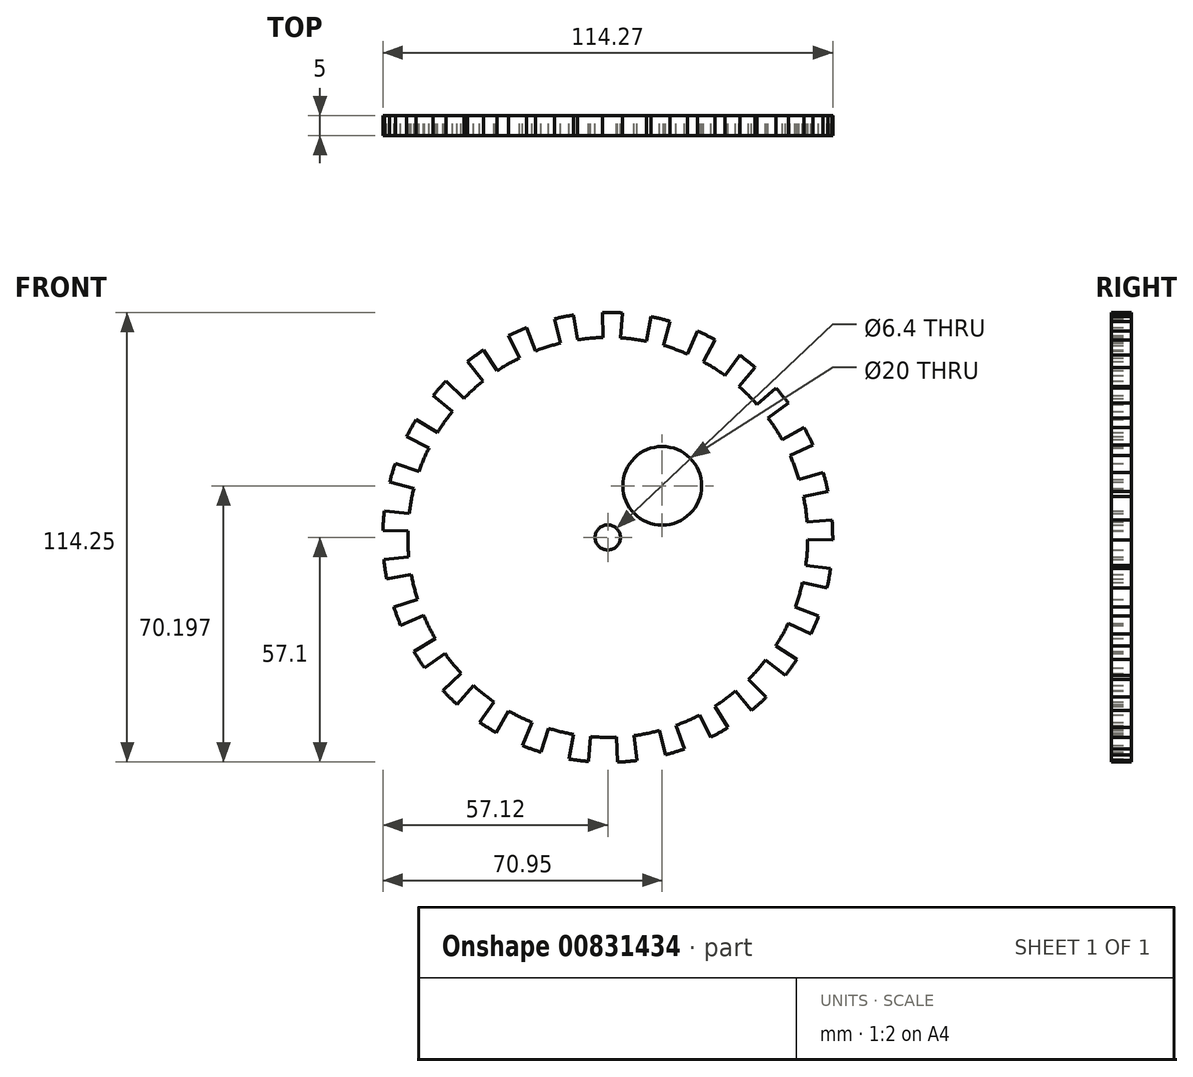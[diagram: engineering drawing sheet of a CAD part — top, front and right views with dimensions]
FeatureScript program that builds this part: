
annotation { "Feature Type Name" : "Feature", "Feature Type Description" : "" }
export const myFeature = defineFeature(function(context is Context, id is Id, definition is map)
    precondition{}
    {
        {
            var Q0;
            Q0=qCreatedBy(makeId("Front.planeOp"),FACE);
            var sketch = newSketch(context, id + "F0", { "sketchPlane" : qUnion([Q0])});
            skArc(sketch, "E0", {"start": v(15.87, 54.9) * mm, "mid": v(13.45, 55.55) * mm, "end": v(11, 56.08) * mm});
            skCircle(sketch, "E1", {"center": v(0, 0) * mm, "radius": 50.8 * mm});
            skLineSegment(sketch, "E2", {"start": v(14.1, 48.8) * mm, "end": v(15.87, 54.9) * mm});
            skLineSegment(sketch, "E3", {"start": v(9.78, 49.85) * mm, "end": v(11, 56.08) * mm});
            skArc(sketch, "E4.1.0", {"start": v(3.7, 57.03) * mm, "mid": v(1.2, 57.14) * mm, "end": v(-1.3, 57.14) * mm});
            skLineSegment(sketch, "E4.1.1", {"start": v(3.28, 50.7) * mm, "end": v(3.7, 57.03) * mm});
            skLineSegment(sketch, "E4.1.2", {"start": v(-1.16, 50.79) * mm, "end": v(-1.3, 57.14) * mm});
            skArc(sketch, "E4.2.0", {"start": v(-8.65, 56.5) * mm, "mid": v(-11.12, 56.06) * mm, "end": v(-13.56, 55.52) * mm});
            skLineSegment(sketch, "E4.2.1", {"start": v(-7.7, 50.21) * mm, "end": v(-8.65, 56.5) * mm});
            skLineSegment(sketch, "E4.2.2", {"start": v(-12.05, 49.35) * mm, "end": v(-13.56, 55.52) * mm});
            skArc(sketch, "E4.3.0", {"start": v(-20.6, 53.3) * mm, "mid": v(-22.9, 52.36) * mm, "end": v(-25.18, 51.3) * mm});
            skLineSegment(sketch, "E4.3.1", {"start": v(-18.3, 47.39) * mm, "end": v(-20.6, 53.3) * mm});
            skLineSegment(sketch, "E4.3.2", {"start": v(-22.38, 45.6) * mm, "end": v(-25.18, 51.3) * mm});
            skArc(sketch, "E4.4.0", {"start": v(-31.57, 47.64) * mm, "mid": v(-33.63, 46.2) * mm, "end": v(-35.62, 44.7) * mm});
            skLineSegment(sketch, "E4.4.1", {"start": v(-28.07, 42.34) * mm, "end": v(-31.57, 47.64) * mm});
            skLineSegment(sketch, "E4.4.2", {"start": v(-31.66, 39.73) * mm, "end": v(-35.62, 44.7) * mm});
            skArc(sketch, "E4.5.0", {"start": v(-41.08, 39.73) * mm, "mid": v(-42.78, 37.9) * mm, "end": v(-44.4, 36) * mm});
            skLineSegment(sketch, "E4.5.1", {"start": v(-36.51, 35.32) * mm, "end": v(-41.08, 39.73) * mm});
            skLineSegment(sketch, "E4.5.2", {"start": v(-39.46, 32) * mm, "end": v(-44.4, 36) * mm});
            skArc(sketch, "E4.6.0", {"start": v(-48.66, 29.98) * mm, "mid": v(-49.92, 27.82) * mm, "end": v(-51.1, 25.6) * mm});
            skLineSegment(sketch, "E4.6.1", {"start": v(-43.25, 26.65) * mm, "end": v(-48.66, 29.98) * mm});
            skLineSegment(sketch, "E4.6.2", {"start": v(-45.41, 22.76) * mm, "end": v(-51.1, 25.6) * mm});
            skArc(sketch, "E4.7.0", {"start": v(-53.96, 18.81) * mm, "mid": v(-54.74, 16.44) * mm, "end": v(-55.4, 14.03) * mm});
            skLineSegment(sketch, "E4.7.1", {"start": v(-47.97, 16.72) * mm, "end": v(-53.96, 18.81) * mm});
            skLineSegment(sketch, "E4.7.2", {"start": v(-49.25, 12.47) * mm, "end": v(-55.4, 14.03) * mm});
            skArc(sketch, "E4.8.0", {"start": v(-56.75, 6.77) * mm, "mid": v(-56.99, 4.29) * mm, "end": v(-57.12, 1.79) * mm});
            skLineSegment(sketch, "E4.8.1", {"start": v(-50.44, 6.02) * mm, "end": v(-56.75, 6.77) * mm});
            skLineSegment(sketch, "E4.8.2", {"start": v(-50.78, 1.59) * mm, "end": v(-57.12, 1.79) * mm});
            skArc(sketch, "E4.9.0", {"start": v(-56.88, -5.58) * mm, "mid": v(-56.58, -8.07) * mm, "end": v(-56.17, -10.53) * mm});
            skLineSegment(sketch, "E4.9.1", {"start": v(-50.56, -4.96) * mm, "end": v(-56.88, -5.58) * mm});
            skLineSegment(sketch, "E4.9.2", {"start": v(-49.93, -9.36) * mm, "end": v(-56.17, -10.53) * mm});
            skArc(sketch, "E4.10.0", {"start": v(-54.35, -17.68) * mm, "mid": v(-53.52, -20.04) * mm, "end": v(-52.6, -22.36) * mm});
            skLineSegment(sketch, "E4.10.1", {"start": v(-48.3, -15.71) * mm, "end": v(-54.35, -17.68) * mm});
            skLineSegment(sketch, "E4.10.2", {"start": v(-46.75, -19.88) * mm, "end": v(-52.6, -22.36) * mm});
            skArc(sketch, "E4.11.0", {"start": v(-49.28, -28.95) * mm, "mid": v(-47.96, -31.08) * mm, "end": v(-46.56, -33.15) * mm});
            skLineSegment(sketch, "E4.11.1", {"start": v(-43.8, -25.73) * mm, "end": v(-49.28, -28.95) * mm});
            skLineSegment(sketch, "E4.11.2", {"start": v(-41.38, -29.46) * mm, "end": v(-46.56, -33.15) * mm});
            skArc(sketch, "E4.12.0", {"start": v(-41.9, -38.86) * mm, "mid": v(-40.16, -40.66) * mm, "end": v(-38.34, -42.38) * mm});
            skLineSegment(sketch, "E4.12.1", {"start": v(-37.24, -34.55) * mm, "end": v(-41.9, -38.86) * mm});
            skLineSegment(sketch, "E4.12.2", {"start": v(-34.08, -37.67) * mm, "end": v(-38.34, -42.38) * mm});
            skArc(sketch, "E4.13.0", {"start": v(-32.57, -46.96) * mm, "mid": v(-30.48, -48.34) * mm, "end": v(-28.34, -49.63) * mm});
            skLineSegment(sketch, "E4.13.1", {"start": v(-28.95, -41.75) * mm, "end": v(-32.57, -46.96) * mm});
            skLineSegment(sketch, "E4.13.2", {"start": v(-25.19, -44.12) * mm, "end": v(-28.34, -49.63) * mm});
            skArc(sketch, "E4.14.0", {"start": v(-21.7, -52.87) * mm, "mid": v(-19.38, -53.77) * mm, "end": v(-17, -54.56) * mm});
            skLineSegment(sketch, "E4.14.1", {"start": v(-19.3, -47) * mm, "end": v(-21.7, -52.87) * mm});
            skLineSegment(sketch, "E4.14.2", {"start": v(-15.12, -48.5) * mm, "end": v(-17, -54.56) * mm});
            skArc(sketch, "E4.15.0", {"start": v(-9.84, -56.3) * mm, "mid": v(-7.36, -56.67) * mm, "end": v(-4.88, -56.94) * mm});
            skLineSegment(sketch, "E4.15.1", {"start": v(-8.74, -50.04) * mm, "end": v(-9.84, -56.3) * mm});
            skLineSegment(sketch, "E4.15.2", {"start": v(-4.34, -50.61) * mm, "end": v(-4.88, -56.94) * mm});
            skArc(sketch, "E4.16.0", {"start": v(2.5, -57.1) * mm, "mid": v(5, -56.93) * mm, "end": v(7.48, -56.66) * mm});
            skLineSegment(sketch, "E4.16.1", {"start": v(2.22, -50.75) * mm, "end": v(2.5, -57.1) * mm});
            skLineSegment(sketch, "E4.16.2", {"start": v(6.65, -50.36) * mm, "end": v(7.48, -56.66) * mm});
            skArc(sketch, "E4.17.0", {"start": v(14.71, -55.22) * mm, "mid": v(17.11, -54.53) * mm, "end": v(19.48, -53.73) * mm});
            skLineSegment(sketch, "E4.17.1", {"start": v(13.08, -49.09) * mm, "end": v(14.71, -55.22) * mm});
            skLineSegment(sketch, "E4.17.2", {"start": v(17.32, -47.76) * mm, "end": v(19.48, -53.73) * mm});
            skArc(sketch, "E4.18.0", {"start": v(26.24, -50.77) * mm, "mid": v(28.43, -49.57) * mm, "end": v(30.58, -48.28) * mm});
            skLineSegment(sketch, "E4.18.1", {"start": v(23.32, -45.13) * mm, "end": v(26.24, -50.77) * mm});
            skLineSegment(sketch, "E4.18.2", {"start": v(27.18, -42.92) * mm, "end": v(30.58, -48.28) * mm});
            skArc(sketch, "E4.19.0", {"start": v(36.54, -43.94) * mm, "mid": v(38.43, -42.3) * mm, "end": v(40.24, -40.58) * mm});
            skLineSegment(sketch, "E4.19.1", {"start": v(32.48, -39.06) * mm, "end": v(36.54, -43.94) * mm});
            skLineSegment(sketch, "E4.19.2", {"start": v(35.77, -36.07) * mm, "end": v(40.24, -40.58) * mm});
            skArc(sketch, "E4.20.0", {"start": v(45.13, -35.06) * mm, "mid": v(46.62, -33.05) * mm, "end": v(48.02, -30.98) * mm});
            skLineSegment(sketch, "E4.20.1", {"start": v(40.12, -31.17) * mm, "end": v(45.13, -35.06) * mm});
            skLineSegment(sketch, "E4.20.2", {"start": v(42.69, -27.54) * mm, "end": v(48.02, -30.98) * mm});
            skArc(sketch, "E4.21.0", {"start": v(51.61, -24.54) * mm, "mid": v(52.64, -22.26) * mm, "end": v(53.56, -19.93) * mm});
            skLineSegment(sketch, "E4.21.1", {"start": v(45.88, -21.81) * mm, "end": v(51.61, -24.54) * mm});
            skLineSegment(sketch, "E4.21.2", {"start": v(47.6, -17.72) * mm, "end": v(53.56, -19.93) * mm});
            skArc(sketch, "E4.22.0", {"start": v(55.68, -12.87) * mm, "mid": v(56.2, -10.42) * mm, "end": v(56.6, -7.95) * mm});
            skLineSegment(sketch, "E4.22.1", {"start": v(49.5, -11.44) * mm, "end": v(55.68, -12.87) * mm});
            skLineSegment(sketch, "E4.22.2", {"start": v(50.3, -7.07) * mm, "end": v(56.6, -7.95) * mm});
            skArc(sketch, "E4.23.0", {"start": v(57.15, -0.6) * mm, "mid": v(57.12, 1.9) * mm, "end": v(56.98, 4.4) * mm});
            skLineSegment(sketch, "E4.23.1", {"start": v(50.8, -0.53) * mm, "end": v(57.15, -0.6) * mm});
            skLineSegment(sketch, "E4.23.2", {"start": v(50.65, 3.9) * mm, "end": v(56.98, 4.4) * mm});
            skArc(sketch, "E4.24.0", {"start": v(55.94, 11.7) * mm, "mid": v(55.37, 14.14) * mm, "end": v(54.7, 16.54) * mm});
            skLineSegment(sketch, "E4.24.1", {"start": v(49.72, 10.4) * mm, "end": v(55.94, 11.7) * mm});
            skLineSegment(sketch, "E4.24.2", {"start": v(48.62, 14.7) * mm, "end": v(54.7, 16.54) * mm});
            skArc(sketch, "E4.25.0", {"start": v(52.12, 23.45) * mm, "mid": v(51.04, 25.7) * mm, "end": v(49.87, 27.92) * mm});
            skLineSegment(sketch, "E4.25.1", {"start": v(46.33, 20.85) * mm, "end": v(52.12, 23.45) * mm});
            skLineSegment(sketch, "E4.25.2", {"start": v(44.33, 24.82) * mm, "end": v(49.87, 27.92) * mm});
            skArc(sketch, "E4.26.0", {"start": v(45.86, 34.1) * mm, "mid": v(44.32, 36.08) * mm, "end": v(42.7, 37.98) * mm});
            skLineSegment(sketch, "E4.26.1", {"start": v(40.76, 30.32) * mm, "end": v(45.86, 34.1) * mm});
            skLineSegment(sketch, "E4.26.2", {"start": v(37.96, 33.76) * mm, "end": v(42.7, 37.98) * mm});
            skArc(sketch, "E4.27.0", {"start": v(37.45, 43.17) * mm, "mid": v(35.53, 44.76) * mm, "end": v(33.54, 46.28) * mm});
            skLineSegment(sketch, "E4.27.1", {"start": v(33.3, 38.37) * mm, "end": v(37.45, 43.17) * mm});
            skLineSegment(sketch, "E4.27.2", {"start": v(29.81, 41.13) * mm, "end": v(33.54, 46.28) * mm});
            skArc(sketch, "E4.28.0", {"start": v(27.3, 50.2) * mm, "mid": v(25.07, 51.36) * mm, "end": v(22.8, 52.4) * mm});
            skLineSegment(sketch, "E4.28.1", {"start": v(24.26, 44.63) * mm, "end": v(27.3, 50.2) * mm});
            skLineSegment(sketch, "E4.28.2", {"start": v(20.27, 46.58) * mm, "end": v(22.8, 52.4) * mm});
            skCircle(sketch, "E5", {"center": v(13.83, 13.1) * mm, "radius": 10 * mm});
            skCircle(sketch, "E6", {"center": v(0, 0) * mm, "radius": 3.2 * mm});
            skSolve(sketch);
        }
        {
            var Q0;
            Q0=makeQuery(id+"F0.imprint","IMPRINT",FACE,{"disambiguationData":[TD([[makeQuery(id+"F0.imprint","IMPRINT",EDGE,{"derivedFrom":sQuery(id+"F0.wireOp",EDGE,"E0")}),1.0]])]});
            var Q1;
            Q1=makeQuery(id+"F0.imprint","IMPRINT",FACE,{"disambiguationData":[TD([[makeQuery(id+"F0.imprint","IMPRINT",EDGE,{"derivedFrom":sQuery(id+"F0.wireOp",EDGE,"E4.24.0")}),1.0]])]});
            var Q2;
            Q2=makeQuery(id+"F0.imprint","IMPRINT",FACE,{"disambiguationData":[TD([[makeQuery(id+"F0.imprint","IMPRINT",EDGE,{"derivedFrom":sQuery(id+"F0.wireOp",EDGE,"E4.25.0")}),1.0]])]});
            var Q3;
            Q3=makeQuery(id+"F0.imprint","IMPRINT",FACE,{"disambiguationData":[TD([[makeQuery(id+"F0.imprint","IMPRINT",EDGE,{"derivedFrom":sQuery(id+"F0.wireOp",EDGE,"E4.26.0")}),1.0]])]});
            var Q4;
            Q4=makeQuery(id+"F0.imprint","IMPRINT",FACE,{"disambiguationData":[TD([[makeQuery(id+"F0.imprint","IMPRINT",EDGE,{"derivedFrom":sQuery(id+"F0.wireOp",EDGE,"E4.27.0")}),1.0]])]});
            var Q5;
            Q5=makeQuery(id+"F0.imprint","IMPRINT",FACE,{"disambiguationData":[TD([[makeQuery(id+"F0.imprint","IMPRINT",EDGE,{"derivedFrom":sQuery(id+"F0.wireOp",EDGE,"E4.28.0")}),1.0]])]});
            var Q6;
            Q6=makeQuery(id+"F0.imprint","IMPRINT",FACE,{"disambiguationData":[TD([[makeQuery(id+"F0.imprint","IMPRINT",EDGE,{"derivedFrom":sQuery(id+"F0.wireOp",EDGE,"E4.1.0")}),1.0]])]});
            var Q7;
            Q7=makeQuery(id+"F0.imprint","IMPRINT",FACE,{"disambiguationData":[TD([[makeQuery(id+"F0.imprint","IMPRINT",EDGE,{"derivedFrom":sQuery(id+"F0.wireOp",EDGE,"E4.2.0")}),1.0]])]});
            var Q8;
            Q8=makeQuery(id+"F0.imprint","IMPRINT",FACE,{"disambiguationData":[TD([[makeQuery(id+"F0.imprint","IMPRINT",EDGE,{"derivedFrom":sQuery(id+"F0.wireOp",EDGE,"E4.3.0")}),1.0]])]});
            var Q9;
            Q9=makeQuery(id+"F0.imprint","IMPRINT",FACE,{"disambiguationData":[TD([[makeQuery(id+"F0.imprint","IMPRINT",EDGE,{"derivedFrom":sQuery(id+"F0.wireOp",EDGE,"E4.4.0")}),1.0]])]});
            var Q10;
            Q10=makeQuery(id+"F0.imprint","IMPRINT",FACE,{"disambiguationData":[TD([[makeQuery(id+"F0.imprint","IMPRINT",EDGE,{"derivedFrom":sQuery(id+"F0.wireOp",EDGE,"E4.5.0")}),1.0]])]});
            var Q11;
            Q11=makeQuery(id+"F0.imprint","IMPRINT",FACE,{"disambiguationData":[TD([[makeQuery(id+"F0.imprint","IMPRINT",EDGE,{"derivedFrom":sQuery(id+"F0.wireOp",EDGE,"E4.6.0")}),1.0]])]});
            var Q12;
            Q12=makeQuery(id+"F0.imprint","IMPRINT",FACE,{"disambiguationData":[TD([[makeQuery(id+"F0.imprint","IMPRINT",EDGE,{"derivedFrom":sQuery(id+"F0.wireOp",EDGE,"E4.7.0")}),1.0]])]});
            var Q13;
            Q13=makeQuery(id+"F0.imprint","IMPRINT",FACE,{"disambiguationData":[TD([[makeQuery(id+"F0.imprint","IMPRINT",EDGE,{"derivedFrom":sQuery(id+"F0.wireOp",EDGE,"E4.8.0")}),1.0]])]});
            var Q14;
            Q14=makeQuery(id+"F0.imprint","IMPRINT",FACE,{"disambiguationData":[TD([[makeQuery(id+"F0.imprint","IMPRINT",EDGE,{"derivedFrom":sQuery(id+"F0.wireOp",EDGE,"E4.9.0")}),1.0]])]});
            var Q15;
            Q15=makeQuery(id+"F0.imprint","IMPRINT",FACE,{"disambiguationData":[TD([[makeQuery(id+"F0.imprint","IMPRINT",EDGE,{"derivedFrom":sQuery(id+"F0.wireOp",EDGE,"E4.10.0")}),1.0]])]});
            var Q16;
            Q16=makeQuery(id+"F0.imprint","IMPRINT",FACE,{"disambiguationData":[TD([[makeQuery(id+"F0.imprint","IMPRINT",EDGE,{"derivedFrom":sQuery(id+"F0.wireOp",EDGE,"E4.11.0")}),1.0]])]});
            var Q17;
            Q17=makeQuery(id+"F0.imprint","IMPRINT",FACE,{"disambiguationData":[TD([[makeQuery(id+"F0.imprint","IMPRINT",EDGE,{"derivedFrom":sQuery(id+"F0.wireOp",EDGE,"E4.12.0")}),1.0]])]});
            var Q18;
            Q18=makeQuery(id+"F0.imprint","IMPRINT",FACE,{"disambiguationData":[TD([[makeQuery(id+"F0.imprint","IMPRINT",EDGE,{"derivedFrom":sQuery(id+"F0.wireOp",EDGE,"E4.13.0")}),1.0]])]});
            var Q19;
            Q19=makeQuery(id+"F0.imprint","IMPRINT",FACE,{"disambiguationData":[TD([[makeQuery(id+"F0.imprint","IMPRINT",EDGE,{"derivedFrom":sQuery(id+"F0.wireOp",EDGE,"E4.14.0")}),1.0]])]});
            var Q20;
            Q20=makeQuery(id+"F0.imprint","IMPRINT",FACE,{"disambiguationData":[TD([[makeQuery(id+"F0.imprint","IMPRINT",EDGE,{"derivedFrom":sQuery(id+"F0.wireOp",EDGE,"E4.15.0")}),1.0]])]});
            var Q21;
            Q21=makeQuery(id+"F0.imprint","IMPRINT",FACE,{"disambiguationData":[TD([[makeQuery(id+"F0.imprint","IMPRINT",EDGE,{"derivedFrom":sQuery(id+"F0.wireOp",EDGE,"E4.16.0")}),1.0]])]});
            var Q22;
            Q22=makeQuery(id+"F0.imprint","IMPRINT",FACE,{"disambiguationData":[TD([[makeQuery(id+"F0.imprint","IMPRINT",EDGE,{"derivedFrom":sQuery(id+"F0.wireOp",EDGE,"E4.17.0")}),1.0]])]});
            var Q23;
            Q23=makeQuery(id+"F0.imprint","IMPRINT",FACE,{"disambiguationData":[TD([[makeQuery(id+"F0.imprint","IMPRINT",EDGE,{"derivedFrom":sQuery(id+"F0.wireOp",EDGE,"E4.18.0")}),1.0]])]});
            var Q24;
            Q24=makeQuery(id+"F0.imprint","IMPRINT",FACE,{"disambiguationData":[TD([[makeQuery(id+"F0.imprint","IMPRINT",EDGE,{"derivedFrom":sQuery(id+"F0.wireOp",EDGE,"E4.19.0")}),1.0]])]});
            var Q25;
            Q25=makeQuery(id+"F0.imprint","IMPRINT",FACE,{"disambiguationData":[TD([[makeQuery(id+"F0.imprint","IMPRINT",EDGE,{"derivedFrom":sQuery(id+"F0.wireOp",EDGE,"E4.20.0")}),1.0]])]});
            var Q26;
            Q26=makeQuery(id+"F0.imprint","IMPRINT",FACE,{"disambiguationData":[TD([[makeQuery(id+"F0.imprint","IMPRINT",EDGE,{"derivedFrom":sQuery(id+"F0.wireOp",EDGE,"E4.21.0")}),1.0]])]});
            var Q27;
            Q27=makeQuery(id+"F0.imprint","IMPRINT",FACE,{"disambiguationData":[TD([[makeQuery(id+"F0.imprint","IMPRINT",EDGE,{"derivedFrom":sQuery(id+"F0.wireOp",EDGE,"E4.22.0")}),1.0]])]});
            var Q28;
            Q28=makeQuery(id+"F0.imprint","IMPRINT",FACE,{"disambiguationData":[TD([[makeQuery(id+"F0.imprint","IMPRINT",EDGE,{"derivedFrom":sQuery(id+"F0.wireOp",EDGE,"E4.23.0")}),1.0]])]});
            var Q29;
            Q29=makeQuery(id+"F0.imprint","IMPRINT",FACE,{"disambiguationData":[TD([[makeQuery(id+"F0.imprint","IMPRINT",EDGE,{"derivedFrom":sQuery(id+"F0.wireOp",EDGE,"E5")}),-1.0]])]});
            extrude(context, id + "F1", {"entities" : qUnion([Q0, Q1, Q2, Q3, Q4, Q5, Q6, Q7, Q8, Q9, Q10, Q11, Q12, Q13, Q14, Q15, Q16, Q17, Q18, Q19, Q20, Q21, Q22, Q23, Q24, Q25, Q26, Q27, Q28, Q29]), "depth" : 5 * mm, "offsetDistance" : 25 * mm});
        }
    });
